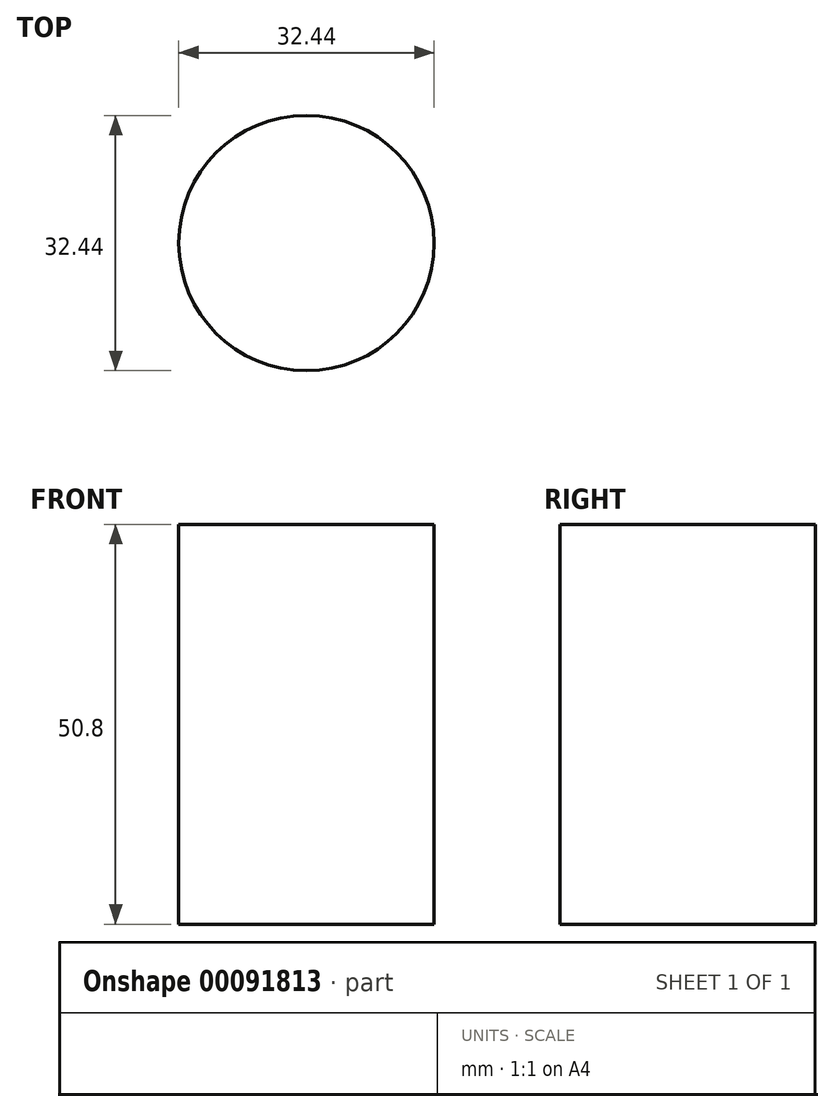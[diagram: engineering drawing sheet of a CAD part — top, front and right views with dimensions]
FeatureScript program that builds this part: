
annotation { "Feature Type Name" : "Feature", "Feature Type Description" : "" }
export const myFeature = defineFeature(function(context is Context, id is Id, definition is map)
    precondition{}
    {
        {
            var Q0;
            Q0=qCreatedBy(makeId("Top.planeOp"),FACE);
            var sketch = newSketch(context, id + "F0", { "sketchPlane" : qUnion([Q0])});
            skCircle(sketch, "E0", {"center": v(0, 0) * mm, "radius": 16.22 * mm});
            skSolve(sketch);
        }
        {
            var Q0;
            Q0=makeQuery(id+"F0.imprint","IMPRINT",FACE,{"disambiguationData":[TD([[makeQuery(id+"F0.imprint","IMPRINT",EDGE,{"derivedFrom":sQuery(id+"F0.wireOp",EDGE,"E0")}),1.0]])]});
            extrude(context, id + "F1", {"entities" : qUnion([Q0]), "depth" : 50.8 * mm});
        }
    });
